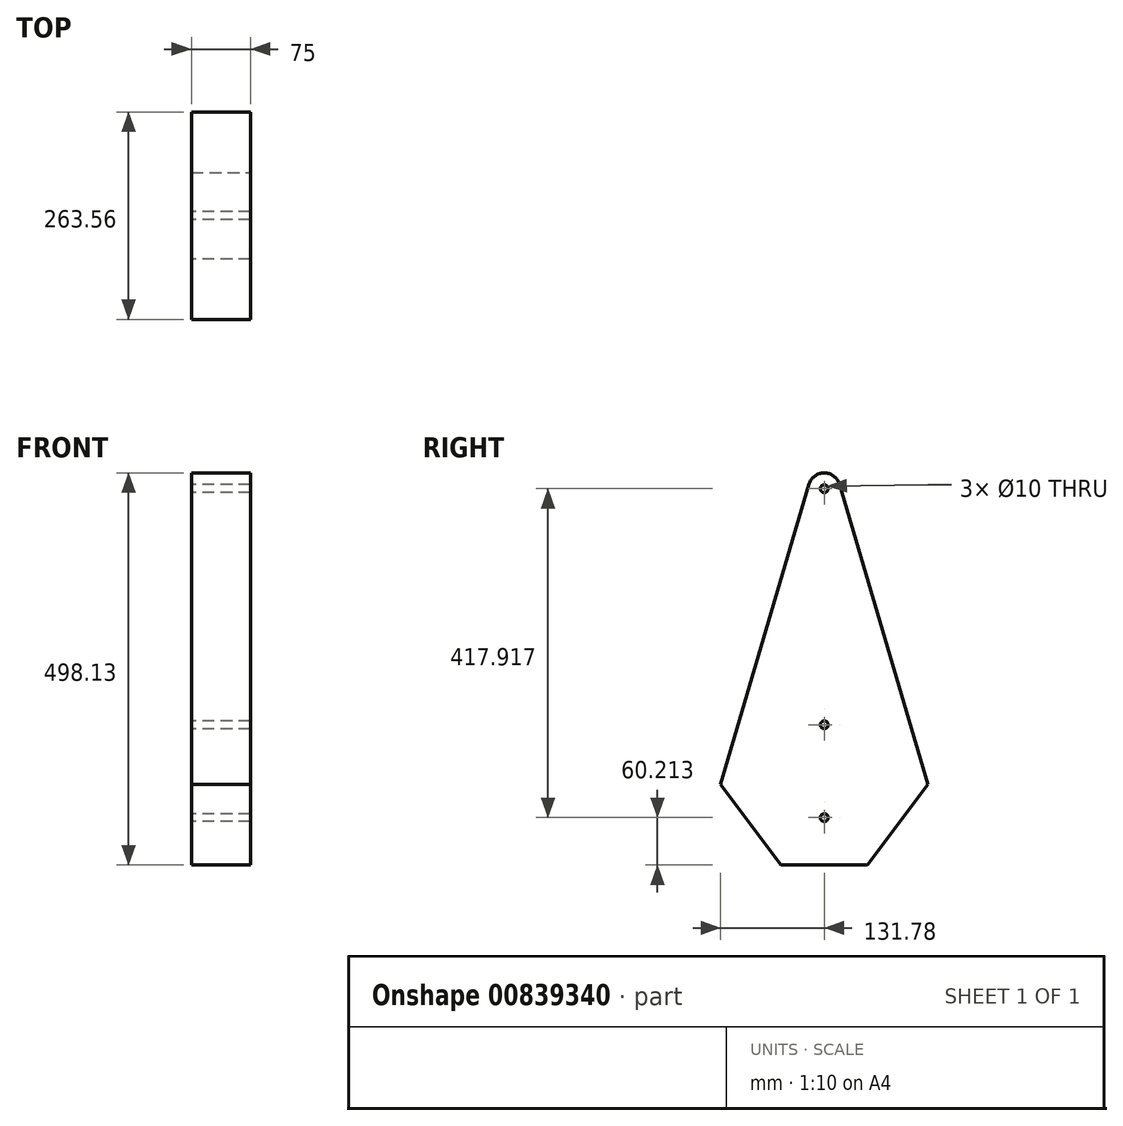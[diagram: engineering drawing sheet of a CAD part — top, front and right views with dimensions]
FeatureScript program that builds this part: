
annotation { "Feature Type Name" : "Feature", "Feature Type Description" : "" }
export const myFeature = defineFeature(function(context is Context, id is Id, definition is map)
    precondition{}
    {
        {
            var Q0;
            Q0=qCreatedBy(makeId("Right.planeOp"),FACE);
            var sketch = newSketch(context, id + "F0", { "sketchPlane" : qUnion([Q0])});
            skLineSegment(sketch, "E0", {"start": v(0, 455.61) * mm, "end": v(0, -178.13) * mm, "construction": true});
            skArc(sketch, "E1", {"start": v(19.18, 305.67) * mm, "mid": v(0, 320) * mm, "end": v(-19.18, 305.67) * mm});
            skCircle(sketch, "E2", {"center": v(0, 0) * mm, "radius": 5 * mm});
            skCircle(sketch, "E3", {"center": v(0, -117.92) * mm, "radius": 5 * mm});
            skCircle(sketch, "E4", {"center": v(0, 300) * mm, "radius": 5 * mm});
            skLineSegment(sketch, "E5", {"start": v(-162.11, -178.13) * mm, "end": v(-19.18, 305.67) * mm});
            skPoint(sketch, "E6.start.orphan", {"position": v(-75, 0) * mm});
            skLineSegment(sketch, "E7.MirrorCS", {"start": v(162.11, -178.13) * mm, "end": v(19.18, 305.67) * mm});
            skPoint(sketch, "E8.MirrorCS.end.orphan", {"position": v(162.11, -178.13) * mm});
            skPoint(sketch, "E8.MirrorCS.start.orphan", {"position": v(75, 0) * mm});
            skLineSegment(sketch, "E9", {"start": v(162.11, -178.13) * mm, "end": v(-162.11, -178.13) * mm});
            skPoint(sketch, "E10.MirrorCS.start.orphan", {"position": v(0, -178.13) * mm});
            skCircle(sketch, "E11", {"center": v(0, 0) * mm, "radius": 105 * mm, "construction": true});
            skSolve(sketch);
        }
        {
            var Q0;
            Q0=makeQuery(id+"F0.imprint","IMPRINT",FACE,{"disambiguationData":[TD([[makeQuery(id+"F0.imprint","IMPRINT",EDGE,{"derivedFrom":sQuery(id+"F0.wireOp",EDGE,"bJJHOdsB-26hl-RVyC-n3W4-FHLlQgOHxvKo")}),1.0]])]});
            var Q1;
            Q1=makeQuery(id+"F0.imprint","IMPRINT",FACE,{"disambiguationData":[TD([[makeQuery(id+"F0.imprint","IMPRINT",EDGE,{"derivedFrom":sQuery(id+"F0.wireOp",EDGE,"E1")}),1.0]])]});
            extrude(context, id + "F1", {"entities" : qUnion([Q0, Q1]), "depth" : 75 * mm, "offsetDistance" : 25 * mm});
        }
        {
            var Q0;
            Q0=makeQuery(id+"F1.opExtrude","SWEPT_EDGE",EDGE,{"disambiguationData":[OSD([sQuery(id+"F0.wireOp",EDGE,"E7.MirrorCS"),sQuery(id+"F0.wireOp",EDGE,"E9")])]});
            var Q1;
            Q1=makeQuery(id+"F1.opExtrude","SWEPT_EDGE",EDGE,{"disambiguationData":[OSD([sQuery(id+"F0.wireOp",EDGE,"E5"),sQuery(id+"F0.wireOp",EDGE,"E9")])]});
            chamfer(context, id + "F2", {"entities" : qUnion([Q0, Q1]), "width" : 80 * mm, "tangentPropagation" : true});
        }
    });
